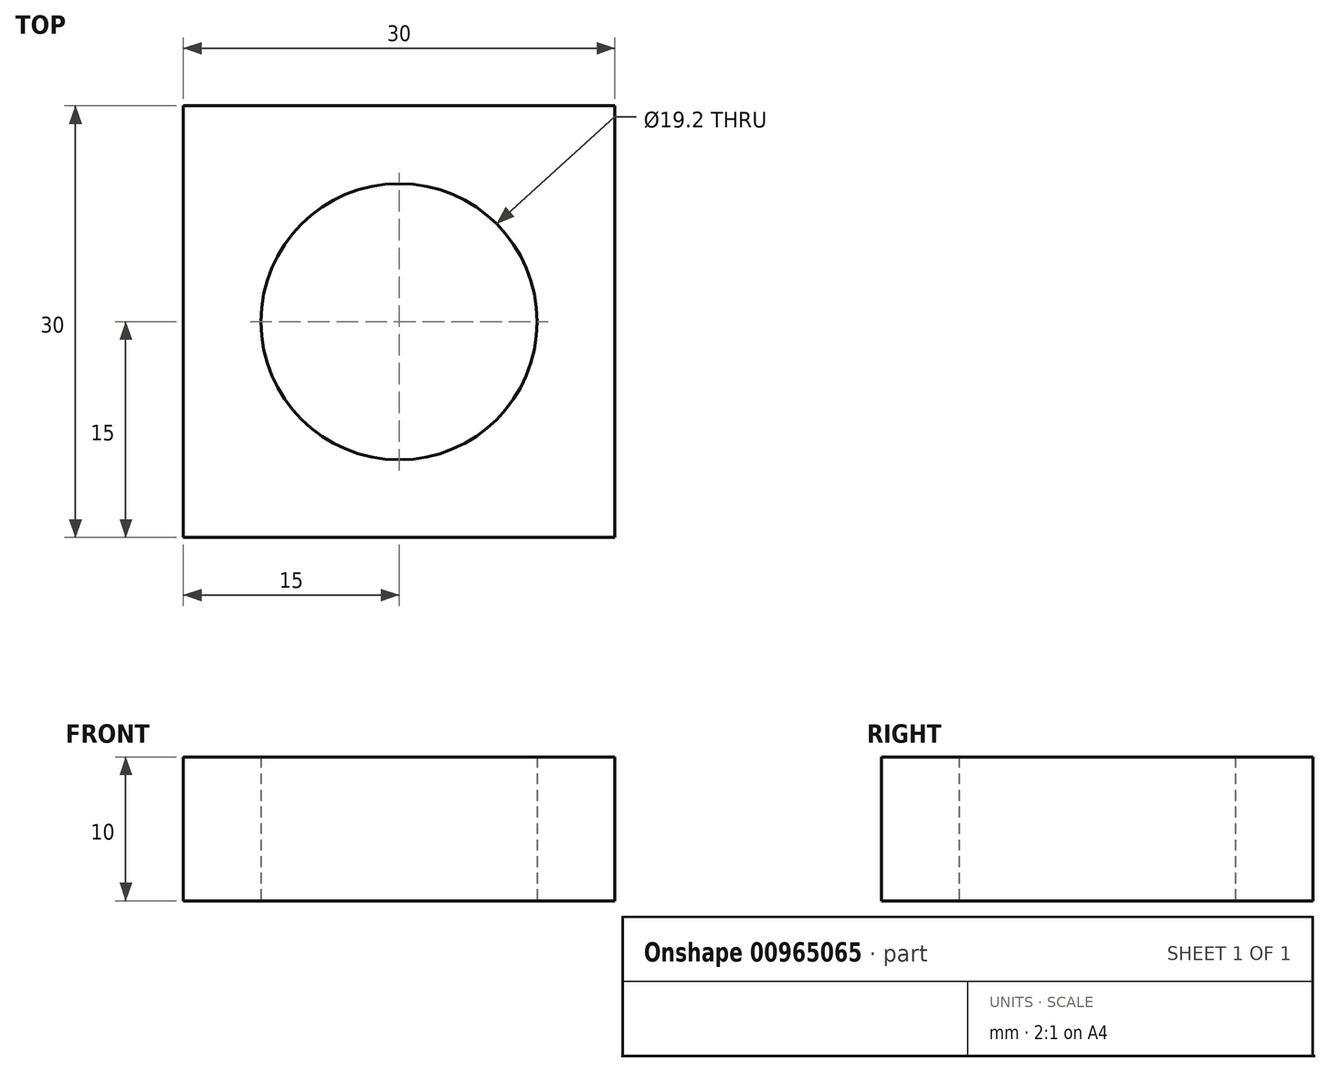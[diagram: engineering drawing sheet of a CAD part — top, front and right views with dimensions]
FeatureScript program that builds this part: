
annotation { "Feature Type Name" : "Feature", "Feature Type Description" : "" }
export const myFeature = defineFeature(function(context is Context, id is Id, definition is map)
    precondition{}
    {
        {
            var Q0;
            Q0=qCreatedBy(makeId("Top.planeOp"),FACE);
            var sketch = newSketch(context, id + "F0", { "sketchPlane" : qUnion([Q0])});
            skCircle(sketch, "E0", {"center": v(0, 0) * mm, "radius": 9.6 * mm});
            skLineSegment(sketch, "E1.bottom", {"start": v(-15, 15) * mm, "end": v(15, 15) * mm});
            skLineSegment(sketch, "E1.top", {"start": v(-15, -15) * mm, "end": v(15, -15) * mm});
            skLineSegment(sketch, "E1.left", {"start": v(-15, 15) * mm, "end": v(-15, -15) * mm});
            skLineSegment(sketch, "E1.right", {"start": v(15, 15) * mm, "end": v(15, -15) * mm});
            skSolve(sketch);
        }
        {
            var Q0;
            Q0=makeQuery(id+"F0.imprint","IMPRINT",FACE,{"disambiguationData":[TD([[makeQuery(id+"F0.imprint","IMPRINT",EDGE,{"derivedFrom":sQuery(id+"F0.wireOp",EDGE,"E0")}),-1.0]])]});
            extrude(context, id + "F1", {"entities" : qUnion([Q0]), "depth" : 10 * mm, "offsetDistance" : 25 * mm});
        }
    });
